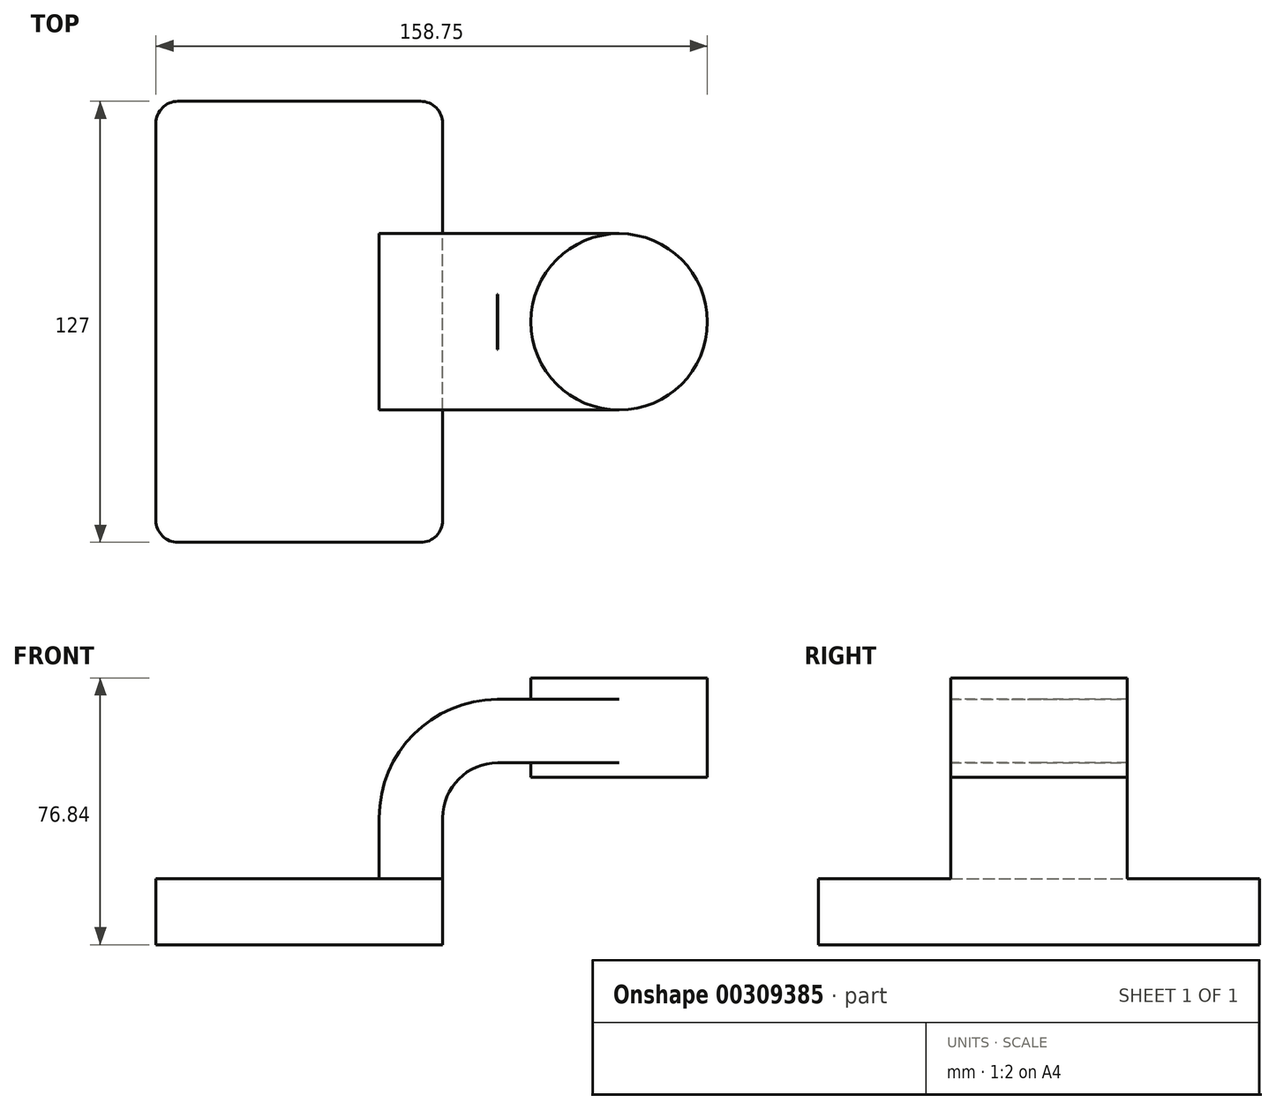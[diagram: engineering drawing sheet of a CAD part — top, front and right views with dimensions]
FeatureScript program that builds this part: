
annotation { "Feature Type Name" : "Feature", "Feature Type Description" : "" }
export const myFeature = defineFeature(function(context is Context, id is Id, definition is map)
    precondition{}
    {
        {
            var Q0;
            Q0=qCreatedBy(makeId("Front.planeOp"),FACE);
            var sketch = newSketch(context, id + "F0", { "sketchPlane" : qUnion([Q0])});
            skLineSegment(sketch, "E0.bottom", {"start": v(41.27, 9.53) * mm, "end": v(-41.28, 9.53) * mm});
            skLineSegment(sketch, "E0.top", {"start": v(41.28, -9.52) * mm, "end": v(-41.27, -9.52) * mm});
            skLineSegment(sketch, "E0.left", {"start": v(41.28, 9.53) * mm, "end": v(41.28, -9.52) * mm});
            skLineSegment(sketch, "E0.right", {"start": v(-41.28, 9.53) * mm, "end": v(-41.27, -9.52) * mm});
            skPoint(sketch, "E0.middle", {"position": v(0, 0) * mm});
            skLineSegment(sketch, "E1.bottom", {"start": v(117.48, 67.31) * mm, "end": v(66.68, 67.31) * mm});
            skLineSegment(sketch, "E1.top", {"start": v(117.48, 38.74) * mm, "end": v(66.67, 38.74) * mm});
            skLineSegment(sketch, "E1.left", {"start": v(117.48, 67.31) * mm, "end": v(117.48, 38.74) * mm});
            skLineSegment(sketch, "E1.right", {"start": v(66.67, 67.31) * mm, "end": v(66.67, 38.74) * mm});
            skPoint(sketch, "E1.middle", {"position": v(92.08, 53.02) * mm});
            skLineSegment(sketch, "E2", {"start": v(41.27, 9.53) * mm, "end": v(41.27, 26.98) * mm});
            skArc(sketch, "E3", {"start": v(41.27, 26.98) * mm, "mid": v(45.92, 38.2) * mm, "end": v(57.15, 42.86) * mm});
            skLineSegment(sketch, "E4", {"start": v(57.15, 42.86) * mm, "end": v(92.08, 42.86) * mm});
            skLineSegment(sketch, "E5.0", {"start": v(57.15, 61.15) * mm, "end": v(92.07, 61.15) * mm});
            skArc(sketch, "E5.1", {"start": v(22.99, 26.98) * mm, "mid": v(33, 51.14) * mm, "end": v(57.15, 61.15) * mm});
            skLineSegment(sketch, "E5.2", {"start": v(22.99, 9.53) * mm, "end": v(22.99, 26.98) * mm});
            skLineSegment(sketch, "E6", {"start": v(92.08, 38.74) * mm, "end": v(92.08, 67.31) * mm});
            skFitSpline(sketch, "E7", {"points": [v(-41.28, 9.53) * mm, v(57.15, 61.15) * mm], "startDerivative": vector(42.27, 127.92) * mm, "endDerivative": vector(143.52, 0.34) * mm});
            skSolve(sketch);
        }
        {
            var Q0;
            Q0=makeQuery(id+"F0.imprint","IMPRINT",FACE,{"disambiguationData":[TD([[makeQuery(id+"F0.imprint","IMPRINT",EDGE,{"derivedFrom":sQuery(id+"F0.wireOp",EDGE,"E0.top")}),-1.0]])]});
            extrude(context, id + "F1", {"entities" : qUnion([Q0]), "endBound" : BoundingType.SYMMETRIC, "depth" : 127 * mm});
        }
        {
            var Q0;
            {var subQ1=sQuery(id+"F0.wireOp",EDGE,"E2");Q0=makeQuery(id+"F0.imprint","IMPRINT",FACE,{"disambiguationData":[TD([[makeQuery(id+"F0.imprint","IMPRINT",EDGE,{"derivedFrom":subQ1}),1.0]])]});}
            var Q1;
            {var subQ0=sQuery(id+"F0.wireOp",EDGE,"E5.0");var subQ1=sQuery(id+"F0.wireOp",EDGE,"E1.right");var subQ2=makeQuery(id+"F0.imprint","INTERSECT",VERTEX,{"derivedFrom":[subQ1,subQ0]});Q1=makeQuery(id+"F0.imprint","IMPRINT",FACE,{"disambiguationData":[TD([[makeQuery(id+"F0.imprint","IMPRINT",EDGE,{"disambiguationData":[TD([[subQ2,-1.0]])],"derivedFrom":subQ1}),1.0]])]});}
            extrude(context, id + "F2", {"entities" : qUnion([Q0, Q1]), "operationType" : NewBodyOperationType.ADD, "endBound" : BoundingType.SYMMETRIC, "depth" : 50.8 * mm});
        }
        {
            var Q0;
            Q0=makeQuery(id+"F0.imprint","IMPRINT",FACE,{"disambiguationData":[TD([[makeQuery(id+"F0.imprint","IMPRINT",EDGE,{"derivedFrom":sQuery(id+"F0.wireOp",EDGE,"E5.1")}),1.0]])]});
            extrude(context, id + "F3", {"entities" : qUnion([Q0]), "endBound" : BoundingType.SYMMETRIC, "depth" : 15.88 * mm});
        }
        {
            var Q0;
            {var subQ4=sQuery(id+"F0.wireOp",EDGE,"E1.left");Q0=makeQuery(id+"F0.imprint","IMPRINT",FACE,{"disambiguationData":[TD([[makeQuery(id+"F0.imprint","IMPRINT",EDGE,{"derivedFrom":subQ4}),-1.0]])]});}
            var Q1;
            Q1=sQuery(id+"F0.wireOp",EDGE,"E6");
            revolve(context, id + "F4", {"operationType" : NewBodyOperationType.ADD, "entities" : qUnion([Q0]), "axis" : qUnion([Q1]), "revolveType" : RevolveType.FULL});
        }
        {
            var Q0;
            Q0=makeQuery(id+"F1.opExtrude","CAP_EDGE",EDGE,{"disambiguationData":[OSD([sQuery(id+"F0.wireOp",EDGE,"E0.right")])],"isStart":false});
            var Q1;
            Q1=makeQuery(id+"F1.opExtrude","CAP_EDGE",EDGE,{"disambiguationData":[OSD([sQuery(id+"F0.wireOp",EDGE,"E0.left")])],"isStart":false});
            var Q2;
            Q2=makeQuery(id+"F1.opExtrude","CAP_EDGE",EDGE,{"disambiguationData":[OSD([sQuery(id+"F0.wireOp",EDGE,"E0.left")])],"isStart":true});
            var Q3;
            Q3=makeQuery(id+"F1.opExtrude","CAP_EDGE",EDGE,{"disambiguationData":[OSD([sQuery(id+"F0.wireOp",EDGE,"E0.right")])],"isStart":true});
            fillet(context, id + "F5", {"entities" : qUnion([Q0, Q1, Q2, Q3]), "radius" : 6.35 * mm, "tangentPropagation" : true, "allowEdgeOverflow" : false});
        }
    });
